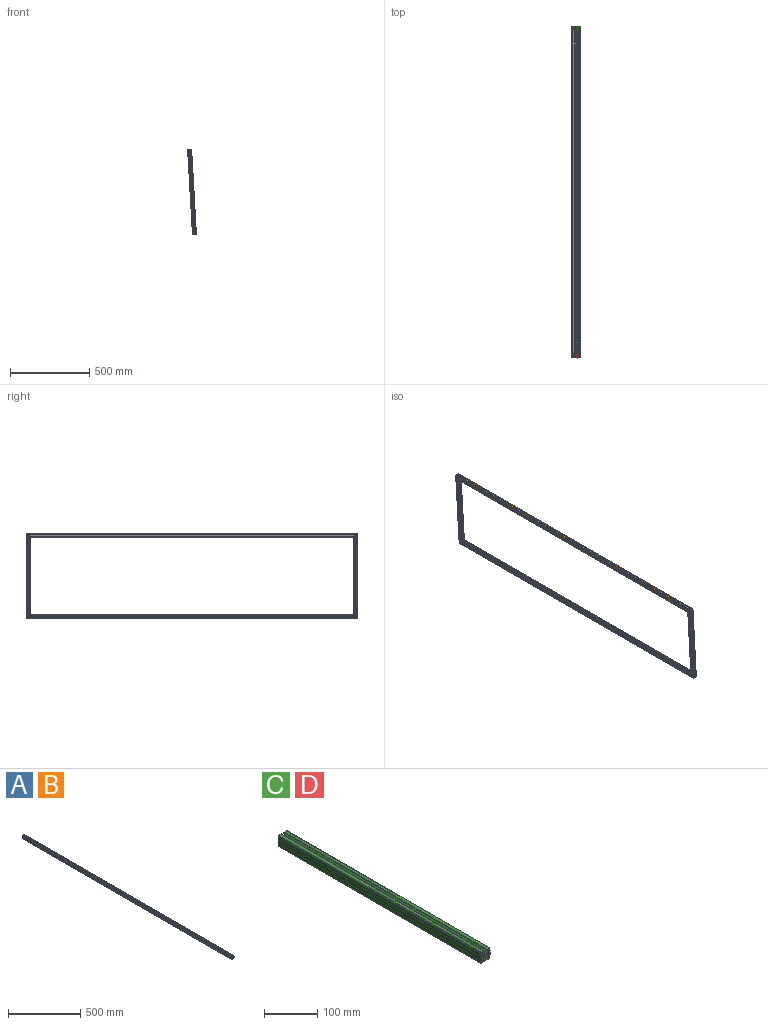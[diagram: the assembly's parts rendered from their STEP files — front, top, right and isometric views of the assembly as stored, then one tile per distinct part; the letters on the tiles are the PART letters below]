
ASSEMBLY  parts=4 mates=3
PART A: 65 faces, bbox 25x2044.7x25 mm
  f0: plane 2044.7x3.11mm, normal (0,0,-1), area 6359mm2, adj f1,f62,f63,f64
  f1: cylinder r=3.17mm len=2044.7mm, axis (0,1,0), area 5086.7mm2, adj f0,f2,f63,f64
  f2: plane 2044.7x3.34mm, normal (-0.71,0,-0.71), area 9646.1mm2, adj f1,f3,f63,f64
  f3: cylinder r=1.01mm len=2044.7mm, axis (0,1,0), area 4866.8mm2, adj f2,f4,f63,f64
  f4: plane 2044.7x2.1mm, normal (0,0,1), area 4293.9mm2, adj f3,f5,f63,f64
  f5: plane 2044.7x8.64mm, normal (0,0,1), area 17666.2mm2, adj f4,f6,f63,f64
  f6: plane 2044.7x2.1mm, normal (0,0,1), area 4293.9mm2, adj f5,f7,f63,f64
  f7: cylinder r=1.01mm len=2044.7mm, axis (0,1,0), area 4866.8mm2, adj f6,f8,f63,f64
  f8: plane 2044.7x3.34mm, normal (0.71,0,-0.71), area 9646.1mm2, adj f7,f62,f63,f64
  f9: plane 2044.7x1.56mm, normal (1,0,0), area 3179.6mm2, adj f10,f59,f63,f64
  f10: plane 2044.7x1.56mm, normal (1,0,0), area 3179.6mm2, adj f9,f11,f63,f64
  f11: cylinder r=3.17mm len=2044.7mm, axis (0,1,0), area 5086.7mm2, adj f10,f12,f63,f64
  f12: plane 2044.7x3.34mm, normal (0.71,0,-0.71), area 9646.1mm2, adj f11,f13,f63,f64
  f13: cylinder r=1.01mm len=2044.7mm, axis (0,1,0), area 4866.8mm2, adj f12,f14,f63,f64
  f14: plane 2044.7x2.1mm, normal (-1,0,0), area 4293.9mm2, adj f13,f15,f63,f64
  f15: plane 2044.7x8.64mm, normal (-1,0,0), area 17666.5mm2, adj f14,f16,f63,f64
  f16: plane 2044.7x2.1mm, normal (-1,0,0), area 4293.9mm2, adj f15,f17,f63,f64
  f17: cylinder r=1.01mm len=2044.7mm, axis (0,1,0), area 4866.8mm2, adj f16,f18,f63,f64
  f18: plane 2044.7x3.34mm, normal (0.71,0,0.71), area 9646.1mm2, adj f17,f59,f63,f64
  f19: cylinder r=1.01mm len=2044.7mm, axis (0,1,0), area 4866.8mm2, adj f20,f60,f63,f64
  f20: plane 2044.7x2.1mm, normal (0,0,-1), area 4293.9mm2, adj f19,f21,f63,f64
  f21: cylinder r=1.07mm len=2044.7mm, axis (0,1,0), area 6871.6mm2, adj f20,f22,f63,f64
  f22: plane 2044.7x6.22mm, normal (0,0,1), area 12712mm2, adj f21,f23,f63,f64
  f23: cylinder r=1.96mm len=2044.7mm, axis (0,1,0), area 3149.2mm2, adj f22,f24,f63,f64
  f24: cylinder r=1.96mm len=2044.7mm, axis (0,1,0), area 3149.2mm2, adj f23,f25,f63,f64
  f25: plane 2044.7x6.22mm, normal (-1,0,0), area 12712mm2, adj f24,f26,f63,f64
  f26: plane 2044.7x8.64mm, normal (-1,0,0), area 17666.5mm2, adj f25,f27,f63,f64
  f27: plane 2044.7x6.22mm, normal (-1,0,0), area 12712mm2, adj f26,f28,f63,f64
  f28: cylinder r=1.96mm len=2044.7mm, axis (0,1,0), area 3149.2mm2, adj f27,f29,f63,f64
  f29: cylinder r=1.96mm len=2044.7mm, axis (0,1,0), area 3149.2mm2, adj f28,f30,f63,f64
  f30: plane 2044.7x6.22mm, normal (0,0,-1), area 12712mm2, adj f29,f31,f63,f64
  f31: plane 2044.7x8.64mm, normal (0,0,-1), area 17666.2mm2, adj f30,f32,f63,f64
  f32: plane 2044.7x6.22mm, normal (0,0,-1), area 12712mm2, adj f31,f33,f63,f64
  f33: cylinder r=1.96mm len=2044.7mm, axis (0,1,0), area 3149.2mm2, adj f32,f34,f63,f64
  f34: cylinder r=1.96mm len=2044.7mm, axis (0,1,0), area 3149.2mm2, adj f33,f35,f63,f64
  f35: plane 2044.7x6.22mm, normal (1,0,0), area 12712mm2, adj f34,f36,f63,f64
  f36: plane 2044.7x8.64mm, normal (1,0,0), area 17666.5mm2, adj f35,f37,f63,f64
  f37: plane 2044.7x6.22mm, normal (1,0,0), area 12712mm2, adj f36,f38,f63,f64
  f38: cylinder r=1.96mm len=2044.7mm, axis (0,1,0), area 3149.2mm2, adj f37,f39,f63,f64
  f39: cylinder r=1.96mm len=2044.7mm, axis (0,1,0), area 3149.2mm2, adj f38,f40,f63,f64
  f40: plane 2044.7x6.22mm, normal (0,0,1), area 12712mm2, adj f39,f41,f63,f64
  f41: cylinder r=1.07mm len=2044.7mm, axis (0,1,0), area 6868.6mm2, adj f40,f42,f63,f64
  f42: plane 2044.7x2.1mm, normal (0,0,-1), area 4293.9mm2, adj f41,f43,f63,f64
  f43: cylinder r=1.01mm len=2044.7mm, axis (0,1,0), area 4866.8mm2, adj f42,f44,f63,f64
  f44: plane 2044.7x3.34mm, normal (-0.71,0,0.71), area 9646.1mm2, adj f43,f45,f63,f64
  f45: cylinder r=3.17mm len=2044.7mm, axis (0,1,0), area 5086.7mm2, adj f44,f46,f63,f64
  f46: plane 2044.7x3.11mm, normal (0,0,1), area 6359mm2, adj f45,f47,f63,f64
  f47: cylinder r=3.17mm len=2044.7mm, axis (0,1,0), area 5086.7mm2, adj f46,f60,f63,f64
  f48: plane 2044.7x1.56mm, normal (-1,0,0), area 3179.6mm2, adj f49,f61,f63,f64
  f49: plane 2044.7x1.56mm, normal (-1,0,0), area 3179.6mm2, adj f48,f50,f63,f64
  f50: cylinder r=3.17mm len=2044.7mm, axis (0,1,0), area 5086.7mm2, adj f49,f51,f63,f64
  f51: plane 2044.7x3.34mm, normal (-0.71,0,0.71), area 9646.1mm2, adj f50,f52,f63,f64
  f52: cylinder r=1.01mm len=2044.7mm, axis (0,1,0), area 4866.8mm2, adj f51,f53,f63,f64
  f53: plane 2044.7x2.1mm, normal (1,0,0), area 4293.9mm2, adj f52,f54,f63,f64
  f54: plane 2044.7x8.64mm, normal (1,0,0), area 17666.5mm2, adj f53,f55,f63,f64
  f55: plane 2044.7x2.1mm, normal (1,0,0), area 4293.9mm2, adj f54,f56,f63,f64
  f56: cylinder r=1.01mm len=2044.7mm, axis (0,1,0), area 4866.8mm2, adj f55,f57,f63,f64
  f57: plane 2044.7x3.34mm, normal (-0.71,0,-0.71), area 9646.1mm2, adj f56,f61,f63,f64
  f58: cylinder r=2.5mm len=2044.7mm, axis (0,1,0), area 32118.1mm2, adj f63,f64
  f59: cylinder r=3.17mm len=2044.7mm, axis (0,1,0), area 5086.7mm2, adj f9,f18,f63,f64
  f60: plane 2044.7x3.34mm, normal (0.71,0,0.71), area 9646.1mm2, adj f19,f47,f63,f64
  f61: cylinder r=3.17mm len=2044.7mm, axis (0,1,0), area 5086.7mm2, adj f48,f57,f63,f64
  f62: cylinder r=3.17mm len=2044.7mm, axis (0,1,0), area 5086.7mm2, adj f0,f8,f63,f64
  f63: plane 25x25mm, normal (0,-1,0), area 318mm2, adj f0,f1,f2,f3,f4,f5,f6,f7
  f64: plane 25x25mm, normal (0,1,0), area 318mm2, adj f0,f1,f2,f3,f4,f5,f6,f7
PART B: same geometry as A
PART C: 92 faces, bbox 25x538.5x25 mm
  f0: cylinder r=3.17mm len=38.59mm, axis (0,1,0), area 94.8mm2, adj f1,f2,f80,f91
  f1: plane 37.61x3.13mm, normal (0,0,-1), area 116.6mm2, adj f0,f4,f80,f91
  f2: plane 538.49x3.35mm, normal (-0.71,0,-0.71), area 2505.2mm2, adj f0,f23,f24,f80,f81,f90,f91
  f3: plane 538.49x3.35mm, normal (0.71,0,-0.71), area 2505.2mm2, adj f4,f22,f28,f80,f81,f90,f91
  f4: cylinder r=3.17mm len=38.59mm, axis (0,1,0), area 94.8mm2, adj f1,f3,f80,f91
  f5: cylinder r=6.6mm len=13.21mm, axis (0,0,-1), area 125.8mm2, adj f10,f11,f12,f15,f16,f17,f18,f19
  f6: plane 487.19x3.12mm, normal (0,0,-1), area 1514.8mm2, adj f22,f23,f81,f90
  f7: plane 492.07x2.11mm, normal (0,0,1), area 1029.3mm2, adj f8,f24,f81,f90
  f8: plane 488.9x8.65mm, normal (0,0,1), area 4214.7mm2, adj f7,f9,f81,f90
  f9: plane 492.07x2.11mm, normal (0,0,1), area 1029.3mm2, adj f8,f28,f81,f90
  f10: plane 39.5x1.56mm, normal (1,0,0), area 61.4mm2, adj f5,f30,f77,f80
  f11: plane 489.08x1.56mm, normal (1,0,0), area 760.5mm2, adj f5,f29,f31,f81
  f12: cylinder r=3.17mm len=40.51mm, axis (0,1,0), area 99.5mm2, adj f5,f30,f32,f80
  f13: plane 538.48x13.26mm, normal (0,0,-1), area 4634.8mm2, adj f14,f50,f80,f81,f85
  f14: plane 538.48x6.25mm, normal (0,0,-1), area 3331.9mm2, adj f13,f51,f80,f81
  f15: plane 487.61x3.11mm, normal (0,0,1), area 1516.1mm2, adj f5,f63,f65,f81
  f16: plane 489.08x1.56mm, normal (-1,0,0), area 760.5mm2, adj f5,f21,f67,f81
  f17: plane 39.5x1.56mm, normal (-1,0,0), area 61.4mm2, adj f5,f18,f66,f80
  f18: cylinder r=3.17mm len=39.79mm, axis (0,1,0), area 98.1mm2, adj f5,f17,f69,f80,f84,f86,f87
  f19: cylinder r=2.5mm len=37.85mm, axis (0,1,0), area 594.5mm2, adj f5,f80
  f20: cylinder r=3.17mm len=489.37mm, axis (0,1,0), area 1216.6mm2, adj f5,f29,f38,f81,f87,f89
  f21: cylinder r=3.17mm len=490.09mm, axis (0,1,0), area 1218mm2, adj f5,f16,f75,f81
  f22: cylinder r=3.17mm len=488.17mm, axis (0,1,0), area 1213.2mm2, adj f3,f6,f81,f90
  f23: cylinder r=3.17mm len=488.17mm, axis (0,1,0), area 1213.2mm2, adj f2,f6,f81,f90
  f24: cylinder r=1.01mm len=538.48mm, axis (0,1,0), area 1280.9mm2, adj f2,f7,f25,f80,f81,f90
  f25: plane 42.49x2.11mm, normal (0,0,1), area 85.2mm2, adj f24,f26,f80,f90
  f26: plane 39.33x8.66mm, normal (0,0,1), area 330.3mm2, adj f25,f27,f80,f90,f91
  f27: plane 42.49x2.11mm, normal (0,0,1), area 85.2mm2, adj f26,f28,f80,f90
  f28: cylinder r=1.01mm len=538.48mm, axis (0,1,0), area 1280.9mm2, adj f3,f9,f27,f80,f81,f90
  f29: plane 489.08x1.56mm, normal (1,0,0), area 760.5mm2, adj f5,f11,f20,f81
  f30: plane 39.5x1.56mm, normal (1,0,0), area 61.4mm2, adj f5,f10,f12,f80
  f31: cylinder r=3.17mm len=490.09mm, axis (0,1,0), area 1218mm2, adj f5,f11,f32,f81
  f32: plane 538.48x3.34mm, normal (0.71,0,-0.71), area 2530.5mm2, adj f5,f12,f31,f33,f80,f81
  f33: cylinder r=1.01mm len=538.48mm, axis (0,1,0), area 1281.7mm2, adj f32,f34,f80,f81
  f34: plane 538.48x2.1mm, normal (-1,0,0), area 1130.8mm2, adj f33,f35,f80,f81
  f35: plane 538.48x8.64mm, normal (-1,0,0), area 4652.5mm2, adj f34,f36,f80,f81
  f36: plane 538.48x2.1mm, normal (-1,0,0), area 1130.8mm2, adj f35,f37,f80,f81
  f37: cylinder r=1.01mm len=538.48mm, axis (0,1,0), area 1281.7mm2, adj f36,f38,f80,f81
  f38: plane 538.48x3.34mm, normal (0.71,0,0.71), area 2525.3mm2, adj f20,f37,f77,f80,f81,f89
  f39: cylinder r=1.01mm len=538.48mm, axis (0,1,0), area 1281.7mm2, adj f40,f78,f80,f81
  f40: plane 538.48x2.1mm, normal (0,0,-1), area 1130.8mm2, adj f39,f41,f80,f81
  f41: cylinder r=1.07mm len=538.48mm, axis (0,1,0), area 1809.7mm2, adj f40,f42,f80,f81
  f42: plane 538.48x6.22mm, normal (0,0,1), area 3347.8mm2, adj f41,f43,f80,f81
  f43: cylinder r=1.96mm len=538.48mm, axis (0,1,0), area 829.3mm2, adj f42,f44,f80,f81
  f44: cylinder r=1.96mm len=538.48mm, axis (0,1,0), area 829.3mm2, adj f43,f45,f80,f81
  f45: plane 538.48x6.22mm, normal (-1,0,0), area 3347.8mm2, adj f44,f46,f80,f81
  f46: plane 538.48x8.64mm, normal (-1,0,0), area 4652.5mm2, adj f45,f47,f80,f81
  f47: plane 538.48x6.22mm, normal (-1,0,0), area 3347.8mm2, adj f46,f48,f80,f81
  f48: cylinder r=1.96mm len=538.48mm, axis (0,1,0), area 829.3mm2, adj f47,f49,f80,f81
  f49: cylinder r=1.96mm len=538.48mm, axis (0,1,0), area 829.3mm2, adj f48,f50,f80,f81
  f50: plane 538.48x6.25mm, normal (0,0,-1), area 3331.9mm2, adj f13,f49,f80,f81
  f51: cylinder r=1.96mm len=538.48mm, axis (0,1,0), area 829.3mm2, adj f14,f52,f80,f81
  f52: cylinder r=1.96mm len=538.48mm, axis (0,1,0), area 829.3mm2, adj f51,f53,f80,f81
  f53: plane 538.48x6.22mm, normal (1,0,0), area 3347.8mm2, adj f52,f54,f80,f81
  f54: plane 538.48x8.64mm, normal (1,0,0), area 4652.5mm2, adj f53,f55,f80,f81
  f55: plane 538.48x6.22mm, normal (1,0,0), area 3347.8mm2, adj f54,f56,f80,f81
  f56: cylinder r=1.96mm len=538.48mm, axis (0,1,0), area 829.3mm2, adj f55,f57,f80,f81
  f57: cylinder r=1.96mm len=538.48mm, axis (0,1,0), area 829.3mm2, adj f56,f58,f80,f81
  f58: plane 538.48x6.22mm, normal (0,0,1), area 3347.8mm2, adj f57,f59,f80,f81
  f59: cylinder r=1.07mm len=538.48mm, axis (0,1,0), area 1808.9mm2, adj f58,f60,f80,f81
  f60: plane 538.48x2.1mm, normal (0,0,-1), area 1130.8mm2, adj f59,f61,f80,f81
  f61: cylinder r=1.01mm len=538.48mm, axis (0,1,0), area 1281.7mm2, adj f60,f62,f80,f81
  f62: plane 538.48x3.34mm, normal (-0.71,0,0.71), area 2540.3mm2, adj f61,f63,f80,f81
  f63: cylinder r=3.17mm len=538.48mm, axis (0,1,0), area 1310.5mm2, adj f5,f15,f62,f64,f80,f81,f83
  f64: plane 38.03x3.11mm, normal (0,0,1), area 117.9mm2, adj f5,f63,f65,f80
  f65: cylinder r=3.17mm len=538.48mm, axis (0,1,0), area 1310.5mm2, adj f5,f15,f64,f78,f80,f81,f82
  f66: plane 39.5x1.56mm, normal (-1,0,0), area 61.4mm2, adj f5,f17,f79,f80
  f67: plane 489.08x1.56mm, normal (-1,0,0), area 760.5mm2, adj f5,f16,f68,f81
  f68: cylinder r=3.17mm len=489.37mm, axis (0,1,0), area 1216.6mm2, adj f5,f67,f69,f81,f84,f87
  f69: plane 538.48x3.34mm, normal (-0.71,0,0.71), area 2525.3mm2, adj f18,f68,f70,f80,f81,f84
  f70: cylinder r=1.01mm len=538.48mm, axis (0,1,0), area 1281.7mm2, adj f69,f71,f80,f81
  f71: plane 538.48x2.1mm, normal (1,0,0), area 1130.8mm2, adj f70,f72,f80,f81
  f72: plane 538.48x8.64mm, normal (1,0,0), area 4652.5mm2, adj f71,f73,f80,f81
  f73: plane 538.48x2.1mm, normal (1,0,0), area 1130.8mm2, adj f72,f74,f80,f81
  f74: cylinder r=1.01mm len=538.48mm, axis (0,1,0), area 1281.7mm2, adj f73,f75,f80,f81
  f75: plane 538.48x3.34mm, normal (-0.71,0,-0.71), area 2530.5mm2, adj f5,f21,f74,f79,f80,f81
  f76: cylinder r=2.5mm len=487.43mm, axis (0,1,0), area 7656.5mm2, adj f5,f81
  f77: cylinder r=3.17mm len=39.79mm, axis (0,1,0), area 98.1mm2, adj f5,f10,f38,f80,f87,f88,f89
  f78: plane 538.48x3.34mm, normal (0.71,0,0.71), area 2540.3mm2, adj f39,f65,f80,f81
  f79: cylinder r=3.17mm len=40.51mm, axis (0,1,0), area 99.5mm2, adj f5,f66,f75,f80
  f80: plane 25x25mm, normal (0,-1,0), area 318mm2, adj f0,f1,f2,f3,f4,f10,f12,f13
  f81: plane 25x25mm, normal (0,1,0), area 318mm2, adj f2,f3,f6,f7,f8,f9,f11,f13
  f82: plane 10.84x2.83mm, normal (0,0,-1), area 21.5mm2, adj f5,f65
  f83: plane 10.84x2.83mm, normal (0,0,-1), area 21.5mm2, adj f5,f63
  f84: bspline ~11.9x11.78mm, area 25.1mm2, adj f18,f68,f69,f86,f87
  f85: cone r=3.96mm half-angle=3deg, axis (0,0,-1), area 230.8mm2, adj f13,f87
  f86: bspline ~11.9x0.67mm, area 0mm2, adj f18,f84,f87
  f87: plane 14.25x13.21mm, normal (0,0,1), area 111.8mm2, adj f5,f18,f20,f68,f77,f84,f85,f86
  f88: bspline ~11.9x0.67mm, area 0mm2, adj f77,f87,f89
  f89: bspline ~12x11.9mm, area 25.1mm2, adj f20,f38,f77,f87,f88
  f90: bspline ~14.47x12.91mm, area 121.3mm2, adj f2,f3,f6,f7,f8,f9,f22,f23
  f91: bspline ~11.9x9.41mm, area 52.8mm2, adj f0,f1,f2,f3,f4,f26,f90
PART D: same geometry as C
PLACE A rot(axis=(0,-1,0),3.2deg) t=(58.1,0,26.87)mm
PLACE B rot(axis=(0,1,0),176.7deg) t=(-65.2,0,650.51)mm
PLACE C rot(axis=(1,-0.03,0.03),90deg) t=(16.62,24.58,609.55)mm
PLACE D rot(axis=(-1,-0.03,-0.03),90deg) t=(47.37,-2069.28,71.9)mm
MATE fastened D.f81 <-> A.f30  axis (0.06,0,-1) through (1.33,-2044.7,69.33)mm
MATE fastened C.f81 <-> B.f30  axis (-0.06,0,1) through (-8.37,0,608.12)mm
MATE fastened A.f32 <-> C.f80  axis (0.06,0,-1) through (22.37,0,70.52)mm
